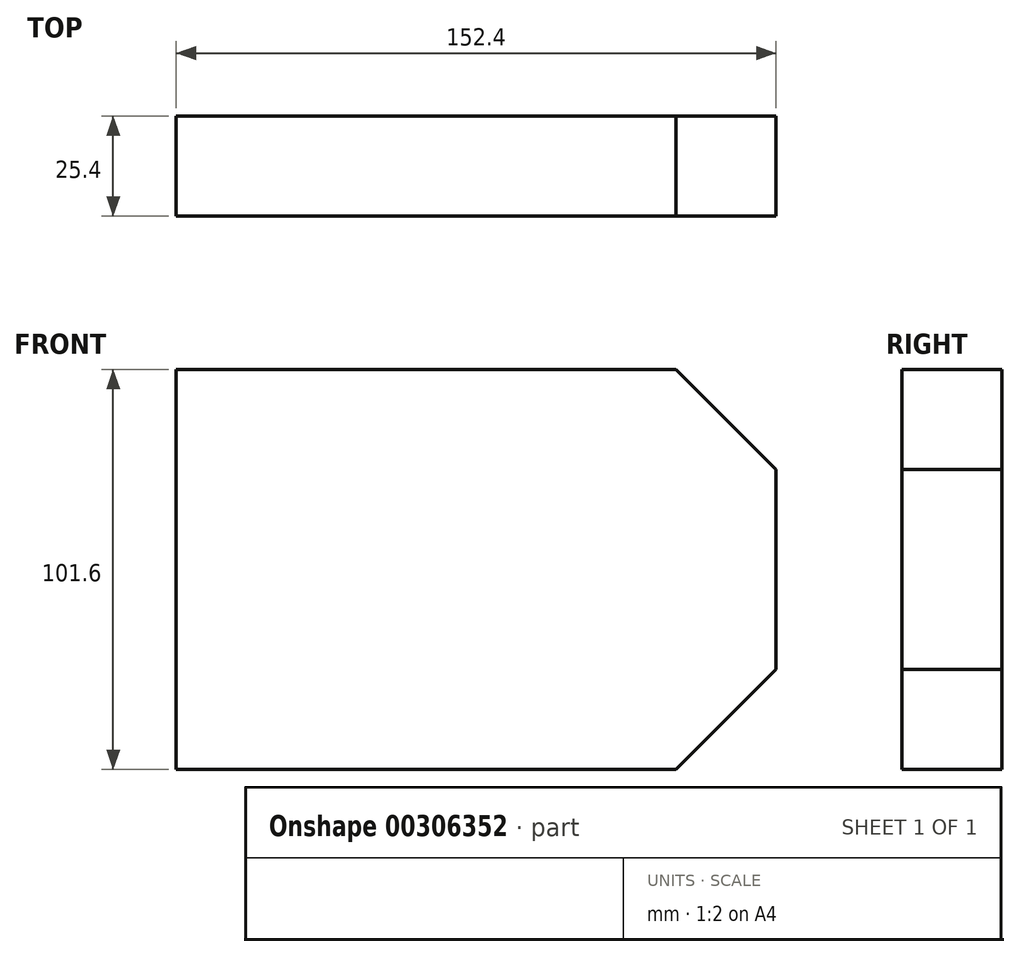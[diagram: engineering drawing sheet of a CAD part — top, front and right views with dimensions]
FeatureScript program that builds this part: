
annotation { "Feature Type Name" : "Feature", "Feature Type Description" : "" }
export const myFeature = defineFeature(function(context is Context, id is Id, definition is map)
    precondition{}
    {
        {
            var Q0;
            Q0=qCreatedBy(makeId("Front.planeOp"),FACE);
            var sketch = newSketch(context, id + "F0", { "sketchPlane" : qUnion([Q0])});
            skLineSegment(sketch, "E0.bottom", {"start": v(76.2, 50.8) * mm, "end": v(-76.2, 50.8) * mm});
            skLineSegment(sketch, "E0.top", {"start": v(76.2, -50.8) * mm, "end": v(-76.2, -50.8) * mm});
            skLineSegment(sketch, "E0.left", {"start": v(76.2, 50.8) * mm, "end": v(76.2, -50.8) * mm});
            skLineSegment(sketch, "E0.right", {"start": v(-76.2, 50.8) * mm, "end": v(-76.2, -50.8) * mm});
            skPoint(sketch, "E0.middle", {"position": v(0, 0) * mm});
            skLineSegment(sketch, "E1", {"start": v(76.2, -25.4) * mm, "end": v(50.8, -50.8) * mm});
            skLineSegment(sketch, "E2", {"start": v(76.2, 25.4) * mm, "end": v(50.8, 50.8) * mm});
            skSolve(sketch);
        }
        {
            var Q0;
            {var subQ0=sQuery(id+"F0.wireOp",EDGE,"E0.right");Q0=makeQuery(id+"F0.imprint","IMPRINT",FACE,{"disambiguationData":[TD([[makeQuery(id+"F0.imprint","IMPRINT",EDGE,{"derivedFrom":subQ0}),1.0]])]});}
            extrude(context, id + "F1", {"entities" : qUnion([Q0]), "depth" : 25.4 * mm});
        }
    });
